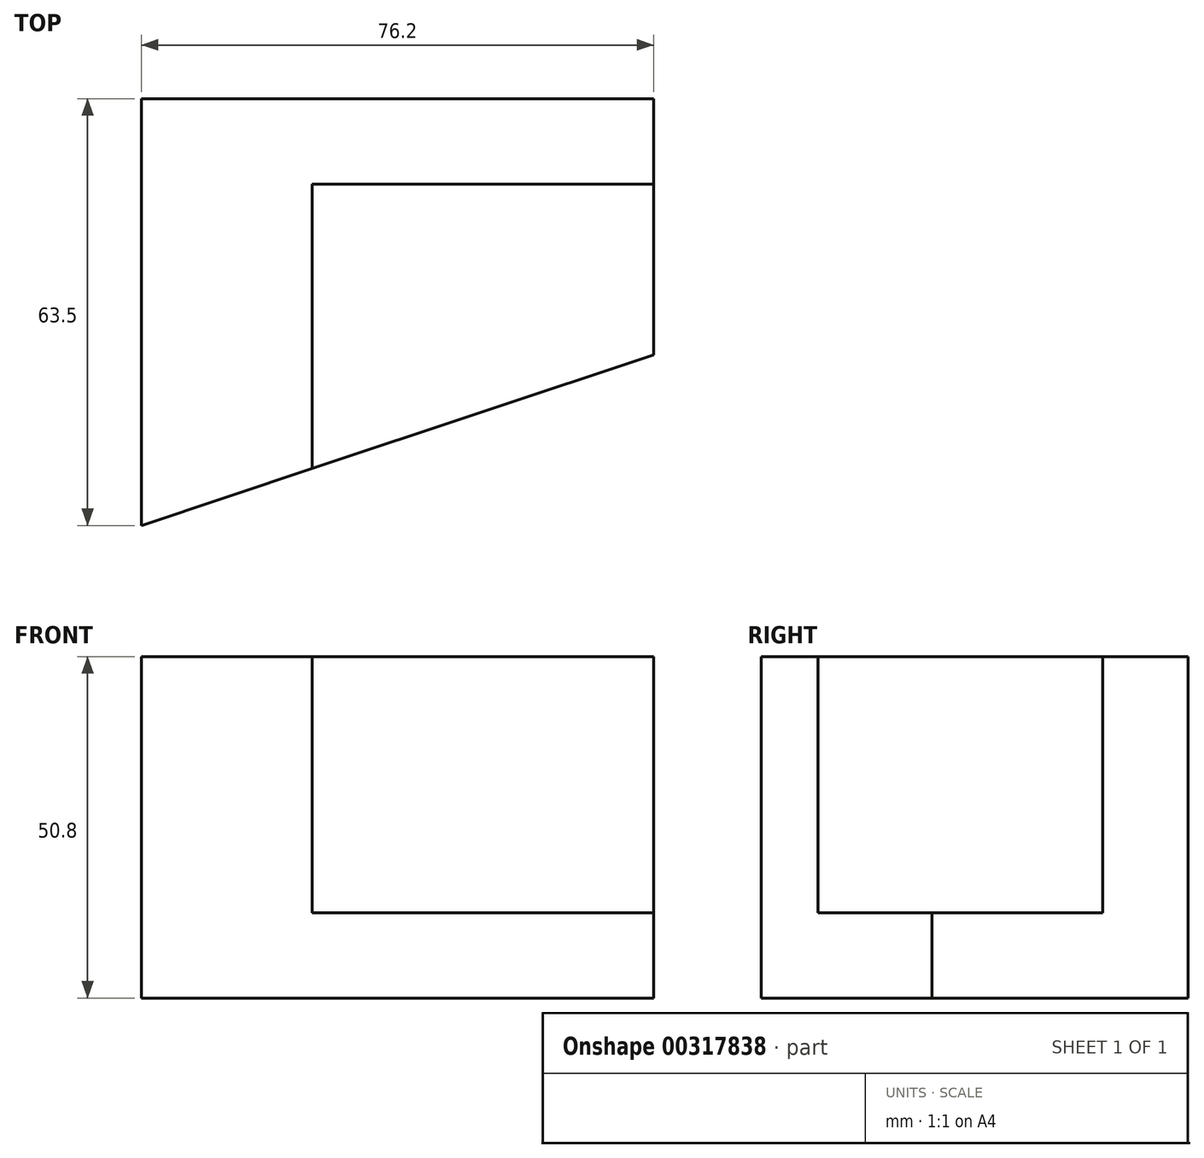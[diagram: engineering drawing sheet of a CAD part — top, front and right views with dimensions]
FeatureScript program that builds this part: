
annotation { "Feature Type Name" : "Feature", "Feature Type Description" : "" }
export const myFeature = defineFeature(function(context is Context, id is Id, definition is map)
    precondition{}
    {
        {
            var Q0;
            Q0=qCreatedBy(makeId("Front.planeOp"),FACE);
            var sketch = newSketch(context, id + "F0", { "sketchPlane" : qUnion([Q0])});
            skLineSegment(sketch, "E0.bottom", {"start": v(0, 0) * mm, "end": v(76.2, 0) * mm});
            skLineSegment(sketch, "E0.top", {"start": v(0, 50.8) * mm, "end": v(76.2, 50.8) * mm});
            skLineSegment(sketch, "E0.left", {"start": v(0, 0) * mm, "end": v(0, 50.8) * mm});
            skLineSegment(sketch, "E0.right", {"start": v(76.2, 0) * mm, "end": v(76.2, 50.8) * mm});
            skSolve(sketch);
        }
        {
            var Q0;
            Q0 = qSketchRegion(id + "F0", true);
            extrude(context, id + "F1", {"entities" : qUnion([Q0]), "depth" : 63.5 * mm});
        }
        {
            var Q0;
            Q0=makeQuery(id+"F1.opExtrude","CAP_FACE",FACE,{"disambiguationData":[OSD([sQuery(id+"F0.wireOp",EDGE,"E0.bottom"),sQuery(id+"F0.wireOp",EDGE,"E0.top"),sQuery(id+"F0.wireOp",EDGE,"E0.left"),sQuery(id+"F0.wireOp",EDGE,"E0.right")])],"isStart":false});
            var sketch = newSketch(context, id + "F2", { "sketchPlane" : qUnion([Q0])});
            skLineSegment(sketch, "E1.bottom", {"start": v(76.2, 50.8) * mm, "end": v(25.4, 50.8) * mm});
            skLineSegment(sketch, "E1.top", {"start": v(76.2, 12.7) * mm, "end": v(25.4, 12.7) * mm});
            skLineSegment(sketch, "E1.left", {"start": v(76.2, 50.8) * mm, "end": v(76.2, 12.7) * mm});
            skLineSegment(sketch, "E1.right", {"start": v(25.4, 50.8) * mm, "end": v(25.4, 12.7) * mm});
            skSolve(sketch);
        }
        {
            var Q0;
            Q0 = qSketchRegion(id + "F2", true);
            extrude(context, id + "F3", {"entities" : qUnion([Q0]), "operationType" : NewBodyOperationType.REMOVE, "oppositeDirection" : true, "depth" : 50.8 * mm});
        }
        {
            var Q0;
            Q0=makeQuery(id+"F1.opExtrude","SWEPT_FACE",FACE,{"disambiguationData":[OSD([sQuery(id+"F0.wireOp",EDGE,"E0.bottom")])]});
            var sketch = newSketch(context, id + "F4", { "sketchPlane" : qUnion([Q0])});
            skLineSegment(sketch, "E2", {"start": v(0, 63.5) * mm, "end": v(76.2, 38.1) * mm});
            skLineSegment(sketch, "E3", {"start": v(76.2, 38.1) * mm, "end": v(76.2, 63.5) * mm});
            skLineSegment(sketch, "E4", {"start": v(76.2, 63.5) * mm, "end": v(0, 63.5) * mm});
            skSolve(sketch);
        }
        {
            var Q0;
            Q0 = qSketchRegion(id + "F4", true);
            extrude(context, id + "F5", {"entities" : qUnion([Q0]), "operationType" : NewBodyOperationType.REMOVE, "endBound" : BoundingType.THROUGH_ALL, "oppositeDirection" : true, "depth" : 25.4 * mm});
        }
    });
